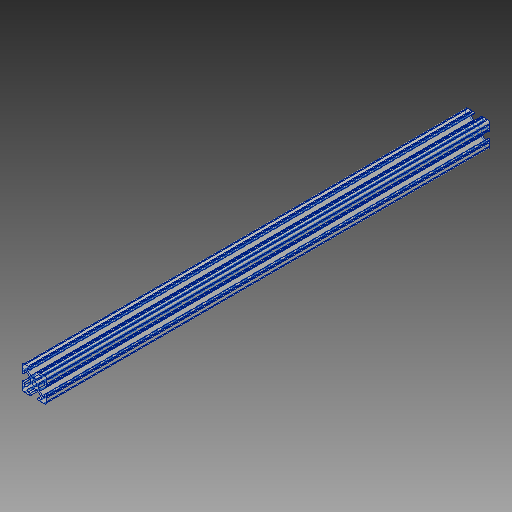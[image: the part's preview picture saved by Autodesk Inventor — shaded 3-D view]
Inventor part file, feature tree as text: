
AUTODESK INVENTOR PART (.ipt)
format: ipt  version: 2019 (Build 230136000, 136)  size: 318,976 bytes
history: native  units: in
note: dims shown in document units (in); Inventor stores cm internally (conversion verified against a paired STEP export)
features: other x1, extrude x1, sketch x1, projected_geometry x1
ambient origin geometry x8: Origin, YZ Plane, XZ Plane, XY Plane, X Axis, Y Axis, Z Axis, Center Point
bodies: Solid1 (feature_tree)
feature tree (4):
  other  "Boss-Extrude1"
  extrude  "Extrusion1"  [1 undecoded]
  sketch  "Sketch1"  dims[d0=6.0in d1=0.0in]
  projected_geometry  "Projected Loop1"
note: 1 required parameter value undecoded (feature->parameter linkage not recoverable at this tier; creation-order binding heuristic only, values carry confidence <= 0.55)
